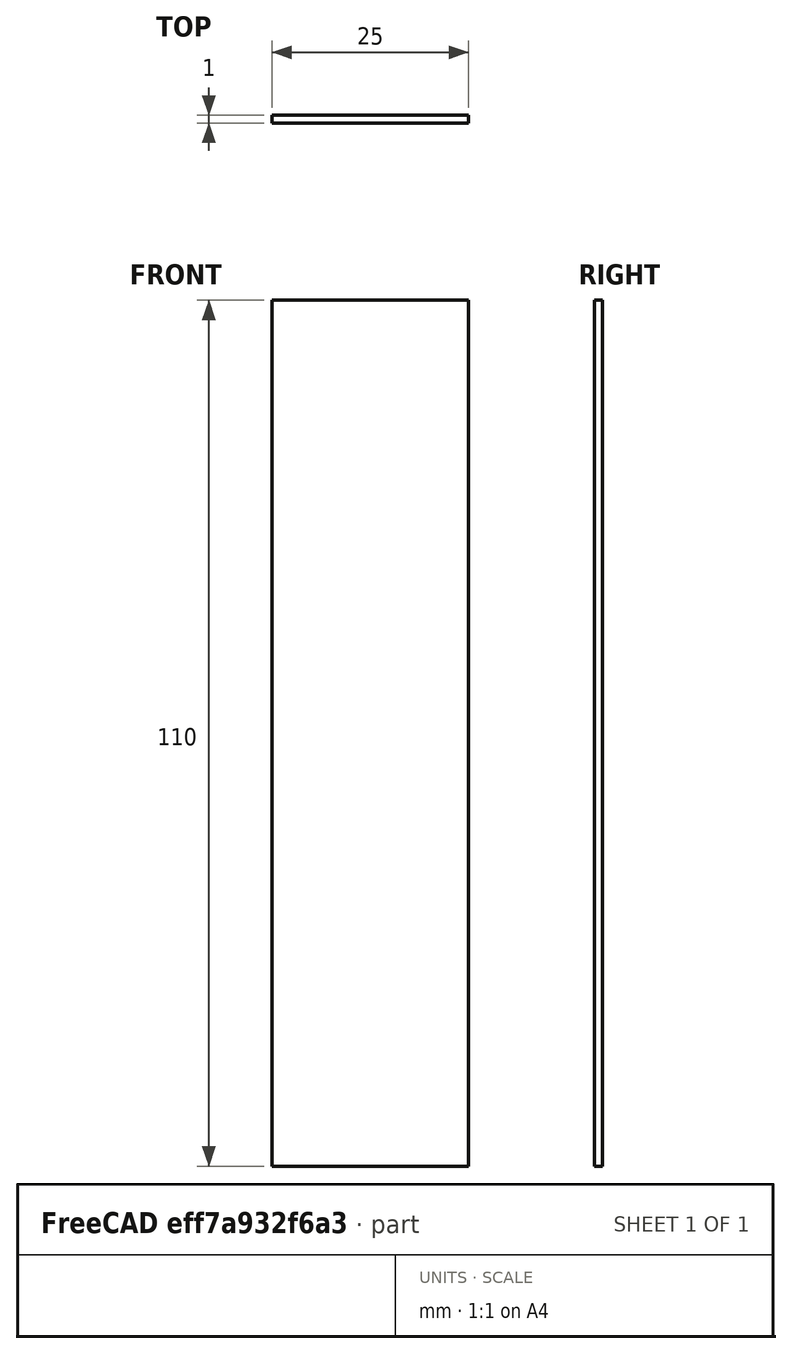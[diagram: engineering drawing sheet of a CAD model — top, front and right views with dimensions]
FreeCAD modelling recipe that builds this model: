
FCSTD DOCUMENT  (FreeCAD 0.19R24366 (Git))
Label: Part1Plate
License: All rights reserved
LicenseURL: http://en.wikipedia.org/wiki/All_rights_reserved
objects: TechDraw::DrawViewDimension×2, Sketcher::SketchObject×1, PartDesign::Pad×1, PartDesign::Body×1, TechDraw::DrawSVGTemplate×1, TechDraw::DrawViewPart×1, TechDraw::DrawPage×1
note: 4 computed .brp shape members not serialized (recipe doc carries the construction recipe); baked Part::Feature solids carry a one-line shape summary decoded from their .brp

FEATURE [Sketcher::SketchObject] Sketch
  FullyConstrained = true
  MapMode = 5
  Placement = pos=(0,0,0) rot=(1,0,0;1.5708rad)
  Support = -> [XZ_Plane]
  sketch-geometry (4):
    g0: LineSegment StartX=-12.5 StartY=55 StartZ=0 EndX=12.5 EndY=55 EndZ=0
    g1: LineSegment StartX=12.5 StartY=55 StartZ=0 EndX=12.5 EndY=-55 EndZ=0
    g2: LineSegment StartX=12.5 StartY=-55 StartZ=0 EndX=-12.5 EndY=-55 EndZ=0
    g3: LineSegment StartX=-12.5 StartY=-55 StartZ=0 EndX=-12.5 EndY=55 EndZ=0
  constraints (12):
    c: Coincident(g0,g1)
    c: Coincident(g1,g2)
    c: Coincident(g2,g3)
    c: Coincident(g3,g0)
    c: Horizontal(g0)
    c: Horizontal(g2)
    c: Vertical(g1)
    c: Vertical(g3)
    c: DistanceX(g0,g0) = 25
    c: DistanceY(g1,g0) = 110
    c: DistanceY(g-1,g0) = 55
    c: DistanceX(g2,g-1) = 12.5
FEATURE [PartDesign::Pad] Pad
  Direction = (1,1,1)
  Length = 1
  Length2 = 100
  Placement = pos=(0,0,0) rot=(1,0,0;1.5708rad)
  Profile = -> Sketch
  Type = 0
FEATURE [PartDesign::Body] Body
  Group = -> [Sketch,Pad]
  Origin = -> Origin
  Tip = -> Pad
FEATURE [TechDraw::DrawSVGTemplate] Template
  EditableTexts = AUTHOR_NAME=Natan Hari Pamungkas; DN=Part - 07; DRAWING_TITLE=Part Plat Besi - 01; FC-DATE=18/03/2022; FC-REV=REV A; FC-SC=1; FC-SH=X / Y; FC-SI=A4; PN=Plate - 01; SI-1=Ketebalan sekitar 1 mm (bisa menyesuaikan); SI-2=Jumlah item 4
  Height = 297
  Orientation = 0
  Width = 210
FEATURE [TechDraw::DrawViewPart] View  label="Front"
  CoarseView = false
  Direction = (0,-1,0)
  Focus = 100
  HardHidden = false
  IsoCount = 0
  IsoHidden = false
  IsoVisible = false
  LockPosition = false
  Perspective = false
  Rotation = 0
  ScaleType = 0
  SeamHidden = false
  SeamVisible = true
  SmoothHidden = false
  SmoothVisible = true
  Source = -> [Body]
  X = 106.79
  XDirection = (1,0,0)
  Y = 176.429
FEATURE [TechDraw::DrawViewDimension] Dimension
  Arbitrary = false
  ArbitraryTolerances = false
  EqualTolerance = true
  FormatSpec = %.2f
  FormatSpecOverTolerance = %+.2f
  FormatSpecUnderTolerance = %+.2f
  Inverted = false
  LockPosition = false
  MeasureType = 1
  OverTolerance = 0
  References2D = -> [View]
  Rotation = 0
  ScaleType = 0
  TheoreticalExact = false
  Type = 1
  UnderTolerance = 0
  X = -1.7903
  Y = 68.6063
FEATURE [TechDraw::DrawViewDimension] Dimension001
  Arbitrary = false
  ArbitraryTolerances = false
  EqualTolerance = true
  FormatSpec = %.2f
  FormatSpecOverTolerance = %+.2f
  FormatSpecUnderTolerance = %+.2f
  Inverted = false
  LockPosition = false
  MeasureType = 1
  OverTolerance = 0
  References2D = -> [View]
  Rotation = 0
  ScaleType = 0
  TheoreticalExact = false
  Type = 2
  UnderTolerance = 0
  X = 31.4772
  Y = 1.7903
FEATURE [TechDraw::DrawPage] Page
  KeepUpdated = true
  NextBalloonIndex = 1
  ProjectionType = 0
  Template = -> Template
  Views = -> [View,Dimension,Dimension001]
